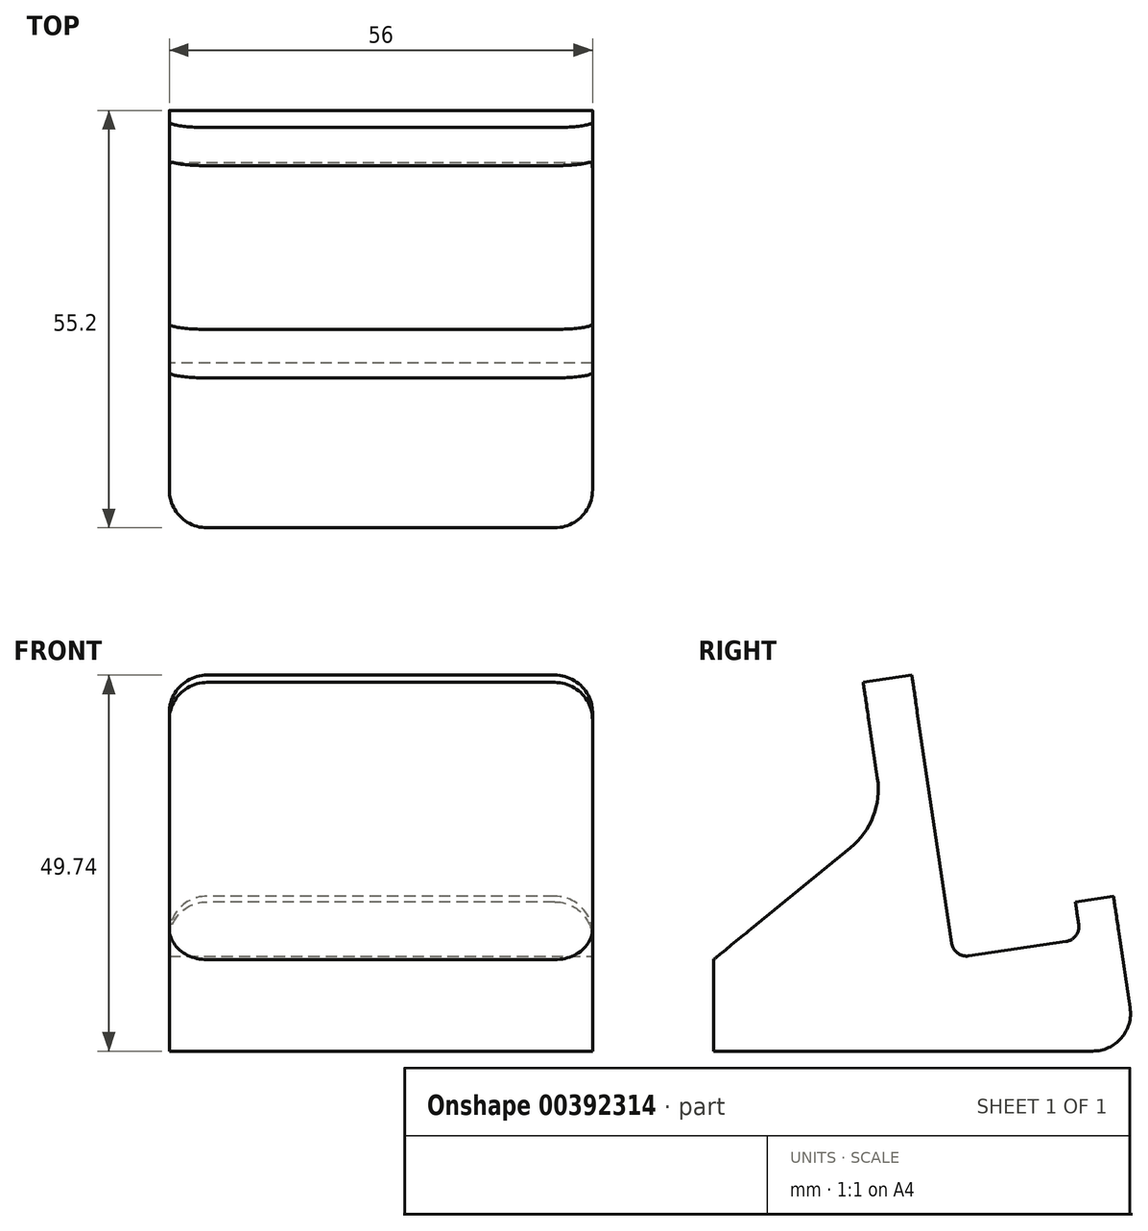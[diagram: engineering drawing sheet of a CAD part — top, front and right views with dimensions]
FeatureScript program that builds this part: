
annotation { "Feature Type Name" : "Feature", "Feature Type Description" : "" }
export const myFeature = defineFeature(function(context is Context, id is Id, definition is map)
    precondition{}
    {
        {
            var Q0;
            Q0=qCreatedBy(makeId("Right.planeOp"),FACE);
            var sketch = newSketch(context, id + "F0", { "sketchPlane" : qUnion([Q0])});
            skLineSegment(sketch, "E0", {"start": v(0, 0) * mm, "end": v(-56, 0) * mm});
            skLineSegment(sketch, "E1", {"start": v(-56, 12.1) * mm, "end": v(-33.46, 30.5) * mm});
            skLineSegment(sketch, "E2", {"start": v(-56, 12.1) * mm, "end": v(-56, 0) * mm});
            skLineSegment(sketch, "E3", {"start": v(0, 0) * mm, "end": v(-3.05, 20.5) * mm});
            skLineSegment(sketch, "E4", {"start": v(-3.05, 20.5) * mm, "end": v(-8.1, 19.75) * mm});
            skLineSegment(sketch, "E5", {"start": v(-8.1, 19.75) * mm, "end": v(-7.36, 14.8) * mm});
            skLineSegment(sketch, "E6", {"start": v(-7.36, 14.8) * mm, "end": v(-24.17, 12.3) * mm});
            skLineSegment(sketch, "E7", {"start": v(-24.17, 12.3) * mm, "end": v(-29.75, 49.74) * mm});
            skLineSegment(sketch, "E8", {"start": v(-29.75, 49.74) * mm, "end": v(-36.18, 48.79) * mm});
            skLineSegment(sketch, "E9", {"start": v(-36.18, 48.79) * mm, "end": v(-33.46, 30.5) * mm});
            skLineSegment(sketch, "E10", {"start": v(0, 0) * mm, "end": v(0, 55.52) * mm, "construction": true});
            skSolve(sketch);
        }
        {
            var Q0;
            Q0=makeQuery(id+"F0.imprint","IMPRINT",FACE,{"disambiguationData":[TD([[makeQuery(id+"F0.imprint","IMPRINT",EDGE,{"derivedFrom":sQuery(id+"F0.wireOp",EDGE,"E0")}),-1.0]])]});
            extrude(context, id + "F1", {"entities" : qUnion([Q0]), "endBound" : BoundingType.SYMMETRIC, "depth" : 56 * mm});
        }
        {
            var Q0;
            Q0=makeQuery(id+"F1.opExtrude","CAP_EDGE",EDGE,{"disambiguationData":[OSD([sQuery(id+"F0.wireOp",EDGE,"E8")])],"isStart":true});
            var Q1;
            Q1=makeQuery(id+"F1.opExtrude","CAP_EDGE",EDGE,{"disambiguationData":[OSD([sQuery(id+"F0.wireOp",EDGE,"E8")])],"isStart":false});
            var Q2;
            Q2=makeQuery(id+"F1.opExtrude","SWEPT_EDGE",EDGE,{"disambiguationData":[OSD([sQuery(id+"F0.wireOp",EDGE,"E0"),sQuery(id+"F0.wireOp",EDGE,"E3")])]});
            var Q3;
            Q3=makeQuery(id+"F1.opExtrude","CAP_EDGE",EDGE,{"disambiguationData":[OSD([sQuery(id+"F0.wireOp",EDGE,"E4")])],"isStart":true});
            var Q4;
            Q4=makeQuery(id+"F1.opExtrude","CAP_EDGE",EDGE,{"disambiguationData":[OSD([sQuery(id+"F0.wireOp",EDGE,"E4")])],"isStart":false});
            fillet(context, id + "F2", {"entities" : qUnion([Q0, Q1, Q2, Q3, Q4]), "radius" : 5 * mm, "tangentPropagation" : true, "allowEdgeOverflow" : false});
        }
        {
            var Q0;
            Q0=makeQuery(id+"F1.opExtrude","CAP_EDGE",EDGE,{"disambiguationData":[OSD([sQuery(id+"F0.wireOp",EDGE,"E2")])],"isStart":true});
            var Q1;
            Q1=makeQuery(id+"F1.opExtrude","CAP_EDGE",EDGE,{"disambiguationData":[OSD([sQuery(id+"F0.wireOp",EDGE,"E2")])],"isStart":false});
            fillet(context, id + "F3", {"entities" : qUnion([Q0, Q1]), "radius" : 5 * mm, "tangentPropagation" : true, "allowEdgeOverflow" : false});
        }
        {
            var Q0;
            Q0=makeQuery(id+"F1.opExtrude","SWEPT_EDGE",EDGE,{"disambiguationData":[OSD([sQuery(id+"F0.wireOp",EDGE,"E1"),sQuery(id+"F0.wireOp",EDGE,"E9")])]});
            fillet(context, id + "F4", {"entities" : qUnion([Q0]), "radius" : 10 * mm, "tangentPropagation" : true, "allowEdgeOverflow" : false});
        }
        {
            var Q0;
            Q0=makeQuery(id+"F1.opExtrude","SWEPT_EDGE",EDGE,{"disambiguationData":[OSD([sQuery(id+"F0.wireOp",EDGE,"E5"),sQuery(id+"F0.wireOp",EDGE,"E6")])]});
            var Q1;
            Q1=makeQuery(id+"F1.opExtrude","SWEPT_EDGE",EDGE,{"disambiguationData":[OSD([sQuery(id+"F0.wireOp",EDGE,"E6"),sQuery(id+"F0.wireOp",EDGE,"E7")])]});
            fillet(context, id + "F5", {"entities" : qUnion([Q0, Q1]), "radius" : 2 * mm, "tangentPropagation" : true, "allowEdgeOverflow" : false});
        }
    });
